# Revit family: KB d=300_Precast-Console Beam_Spæncom
name_source: partatom
category: Structural Framing
revit_build: Autodesk Revit 2014 (Build: 20130308_1515(x64)
units: mm (PartAtom-declared; Revit-internal decimal feet)

## types (9) — shared parameters
Base width = 500 mm  [stored 1.64042 ft]
Height console = 300 mm
Manufacturer = Spæncom
Width (bjælkekroppen) = 275 mm
Width console = 150 mm

## per-type parameters (varying)
| type | Height (bjælkekroppen) | Height element |
| KB48/18 | 180 mm  [stored 0.590551 ft] | 480 mm  [stored 1.5748 ft] |
| KB52/22 | 220 mm  [stored 0.721785 ft] | 520 mm  [stored 1.70604 ft] |
| KB57/27 | 270 mm  [stored 0.885827 ft] | 570 mm  [stored 1.87008 ft] |
| KB60/30 | 300 mm | 600 mm |
| KB62/32 | 320 mm  [stored 1.04987 ft] | 620 mm  [stored 2.03412 ft] |
| KB67/37 | 370 mm  [stored 1.21391 ft] | 670 mm  [stored 2.19816 ft] |
| KB70/40 | 400 mm  [stored 1.31234 ft] | 700 mm  [stored 2.29659 ft] |
| KB80/50 | 500 mm  [stored 1.64042 ft] | 800 mm  [stored 2.62467 ft] |
| KB90/60 | 600 mm | 900 mm  [stored 2.95276 ft] |

note: column(s) folded — value = type name in every type: Model

note: [stored X ft] marks values corroborated as IEEE doubles in the binary element streams (Revit-internal decimal feet)

## geometry (parser evidence)
native form markers: Sweep x1
no freeform markers — native parametric forms only
